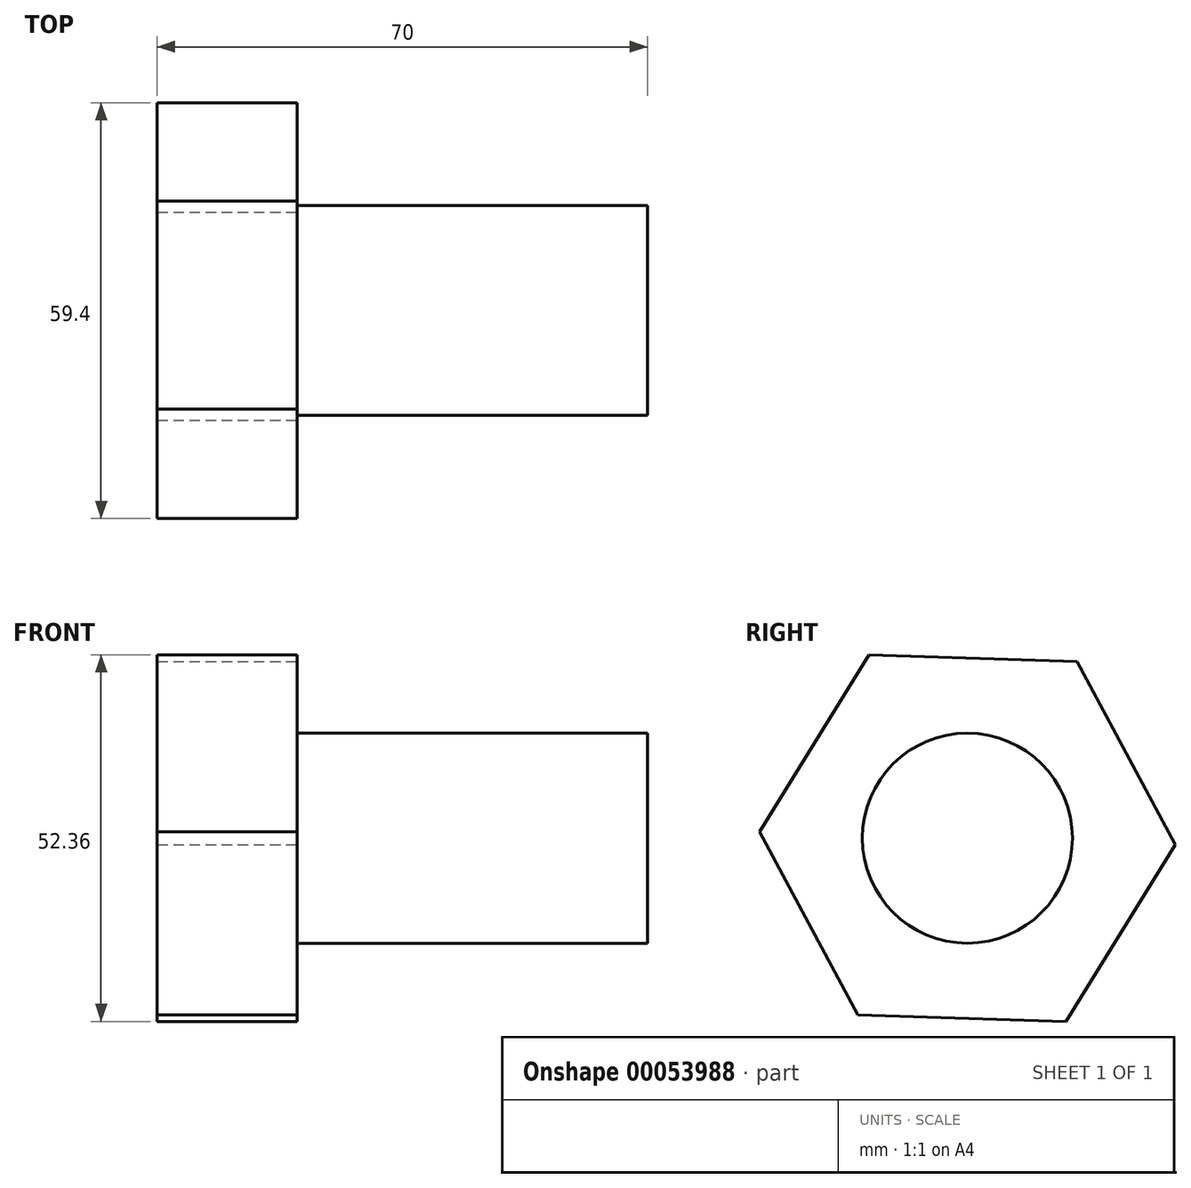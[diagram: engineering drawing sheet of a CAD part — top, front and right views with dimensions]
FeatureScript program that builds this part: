
annotation { "Feature Type Name" : "Feature", "Feature Type Description" : "" }
export const myFeature = defineFeature(function(context is Context, id is Id, definition is map)
    precondition{}
    {
        {
            var Q0;
            Q0=qCreatedBy(makeId("Right.planeOp"),FACE);
            var sketch = newSketch(context, id + "F0", { "sketchPlane" : qUnion([Q0])});
            skCircle(sketch, "E0.cCircle", {"center": v(0, 0) * mm, "radius": 29.72 * mm, "construction": true});
            skLineSegment(sketch, "E0.0", {"start": v(14.05, -26.18) * mm, "end": v(-15.65, -25.26) * mm});
            skLineSegment(sketch, "E0.1", {"start": v(-15.65, -25.26) * mm, "end": v(-29.7, 0.92) * mm});
            skLineSegment(sketch, "E0.2", {"start": v(-29.7, 0.92) * mm, "end": v(-14.05, 26.18) * mm});
            skLineSegment(sketch, "E0.3", {"start": v(-14.05, 26.18) * mm, "end": v(15.65, 25.26) * mm});
            skLineSegment(sketch, "E0.4", {"start": v(15.65, 25.26) * mm, "end": v(29.7, -0.92) * mm});
            skLineSegment(sketch, "E0.5", {"start": v(29.7, -0.92) * mm, "end": v(14.05, -26.18) * mm});
            skSolve(sketch);
        }
        {
            var Q0;
            Q0=makeQuery(id+"F0.imprint","IMPRINT",FACE,{"disambiguationData":[TD([[makeQuery(id+"F0.imprint","IMPRINT",EDGE,{"derivedFrom":sQuery(id+"F0.wireOp",EDGE,"E0.0")}),-1.0]])]});
            extrude(context, id + "F1", {"entities" : qUnion([Q0]), "oppositeDirection" : true, "depth" : 20 * mm});
        }
        {
            var Q0;
            Q0=makeQuery(id+"F1.opExtrude","CAP_FACE",FACE,{"disambiguationData":[OSD([sQuery(id+"F0.wireOp",EDGE,"E0.0"),sQuery(id+"F0.wireOp",EDGE,"E0.1"),sQuery(id+"F0.wireOp",EDGE,"E0.2"),sQuery(id+"F0.wireOp",EDGE,"E0.3"),sQuery(id+"F0.wireOp",EDGE,"E0.4"),sQuery(id+"F0.wireOp",EDGE,"E0.5")])],"isStart":true});
            var sketch = newSketch(context, id + "F2", { "sketchPlane" : qUnion([Q0])});
            skCircle(sketch, "E1", {"center": v(0, 0) * mm, "radius": 15 * mm});
            skSolve(sketch);
        }
        {
            var Q0;
            Q0=makeQuery(id+"F2.imprint","IMPRINT",FACE,{"disambiguationData":[TD([[makeQuery(id+"F2.imprint","IMPRINT",EDGE,{"derivedFrom":sQuery(id+"F2.wireOp",EDGE,"E1")}),1.0]])]});
            extrude(context, id + "F3", {"entities" : qUnion([Q0]), "operationType" : NewBodyOperationType.ADD, "depth" : 50 * mm});
        }
    });
